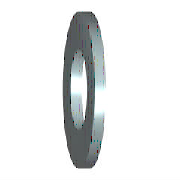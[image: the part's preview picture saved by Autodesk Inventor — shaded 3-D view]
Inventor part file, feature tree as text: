
AUTODESK INVENTOR PART (.ipt)
format: ipt  version: 2016 (Build 200138000, 138)  size: 112,128 bytes
history: native  units: mm (DEFAULTED — no unit token found)
features: other x1, plane x1, sketch x1
ambient origin geometry x7: Origin, YZ Plane, XY Plane, X Axis, Y Axis, Z Axis, Center Point
bodies: Solid1 (feature_tree), Body (feature_tree)
feature tree (3):
  other  "Work Axis1"
  plane  "Work Plane1"
  sketch  "Sketch"  dims[d0=6.4mm d1=12.0mm d2=1.6mm d3=0.0mm d4=0.0mm d5=0.0mm d6=0.0mm d7=0.0mm]
